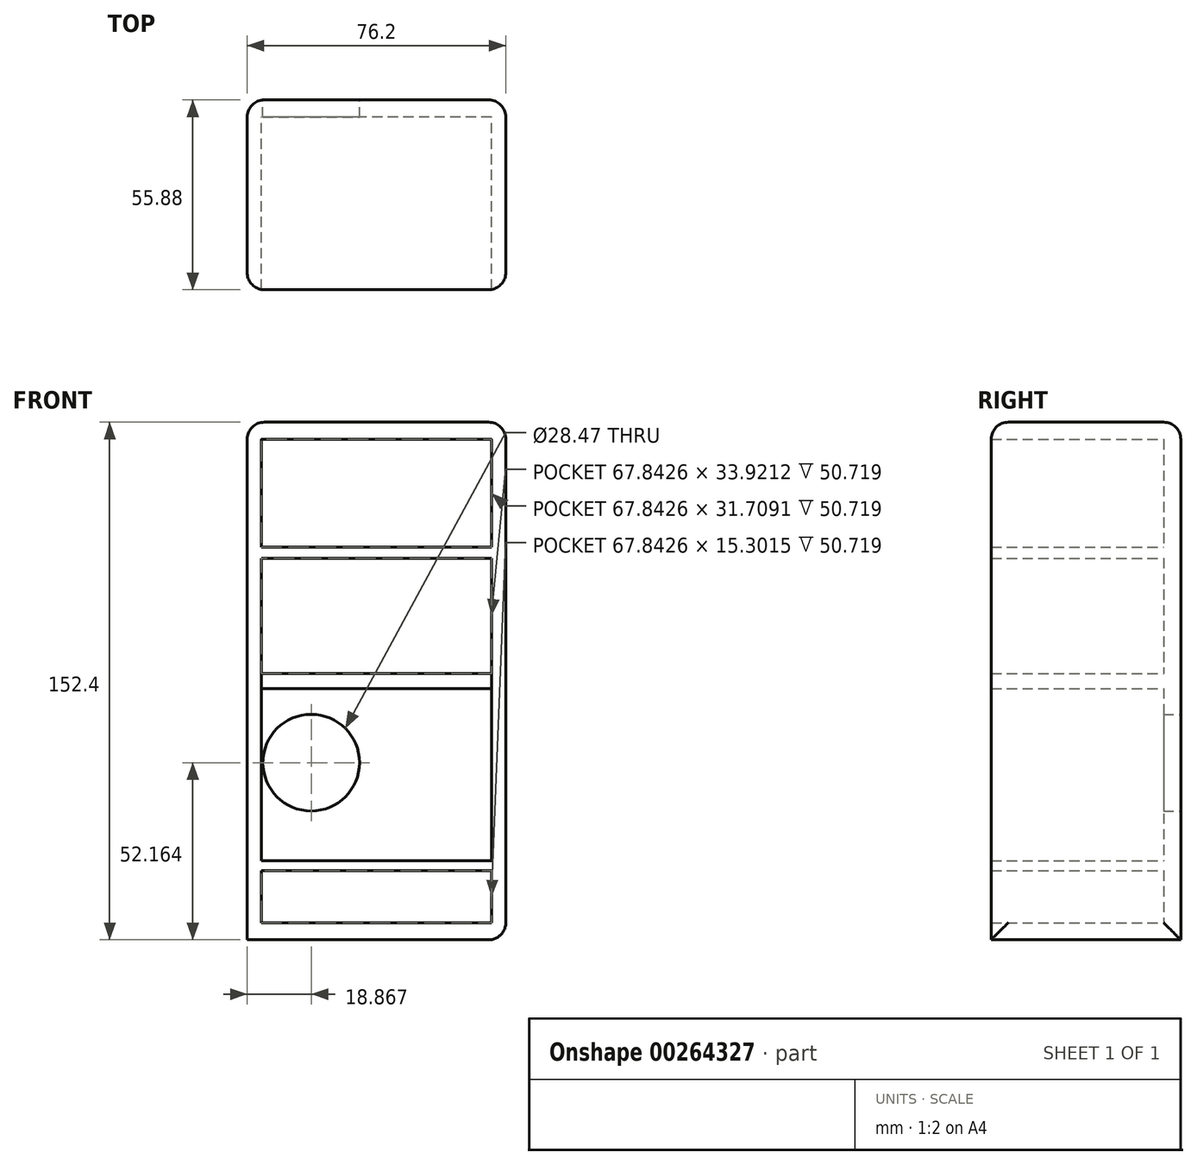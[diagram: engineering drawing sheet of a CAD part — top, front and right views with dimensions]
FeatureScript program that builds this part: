
annotation { "Feature Type Name" : "Feature", "Feature Type Description" : "" }
export const myFeature = defineFeature(function(context is Context, id is Id, definition is map)
    precondition{}
    {
        {
            var Q0;
            Q0=qCreatedBy(makeId("Front.planeOp"),FACE);
            var sketch = newSketch(context, id + "F0", { "sketchPlane" : qUnion([Q0])});
            skLineSegment(sketch, "E0.bottom", {"start": v(38.1, 76.2) * mm, "end": v(-38.1, 76.2) * mm});
            skLineSegment(sketch, "E0.top", {"start": v(38.1, -76.2) * mm, "end": v(-38.1, -76.2) * mm});
            skLineSegment(sketch, "E0.left", {"start": v(38.1, 76.2) * mm, "end": v(38.1, -76.2) * mm});
            skLineSegment(sketch, "E0.right", {"start": v(-38.1, 76.2) * mm, "end": v(-38.1, -76.2) * mm});
            skPoint(sketch, "E0.middle", {"position": v(0, 0) * mm});
            skLineSegment(sketch, "E1.bottom", {"start": v(33.92, 71.16) * mm, "end": v(-33.92, 71.16) * mm});
            skLineSegment(sketch, "E1.top", {"start": v(33.92, -71.16) * mm, "end": v(-33.92, -71.16) * mm});
            skLineSegment(sketch, "E1.left", {"start": v(33.92, 71.16) * mm, "end": v(33.92, -71.16) * mm});
            skLineSegment(sketch, "E1.right", {"start": v(-33.92, 71.16) * mm, "end": v(-33.92, -71.16) * mm});
            skLineSegment(sketch, "E2", {"start": v(-33.92, 39.45) * mm, "end": v(33.92, 39.45) * mm});
            skLineSegment(sketch, "E3", {"start": v(33.92, 39.45) * mm, "end": v(33.92, 36.13) * mm});
            skLineSegment(sketch, "E4", {"start": v(33.92, 36.13) * mm, "end": v(-33.92, 36.13) * mm});
            skLineSegment(sketch, "E5", {"start": v(-33.92, 36.13) * mm, "end": v(-33.92, -55.86) * mm});
            skLineSegment(sketch, "E6", {"start": v(-33.92, -55.86) * mm, "end": v(33.92, -55.86) * mm});
            skLineSegment(sketch, "E7", {"start": v(33.92, -55.86) * mm, "end": v(33.92, -52.9) * mm});
            skLineSegment(sketch, "E8", {"start": v(33.92, -52.9) * mm, "end": v(-33.92, -52.9) * mm});
            skSolve(sketch);
        }
        {
            var Q0;
            Q0=makeQuery(id+"F0.imprint","IMPRINT",FACE,{"disambiguationData":[TD([[makeQuery(id+"F0.imprint","IMPRINT",EDGE,{"derivedFrom":sQuery(id+"F0.wireOp",EDGE,"E0.bottom")}),1.0]])]});
            var Q1;
            {var subQ0=sQuery(id+"F0.wireOp",EDGE,"E2");Q1=makeQuery(id+"F0.imprint","IMPRINT",FACE,{"disambiguationData":[TD([[makeQuery(id+"F0.imprint","IMPRINT",EDGE,{"derivedFrom":subQ0}),-1.0]])]});}
            var Q2;
            {var subQ0=sQuery(id+"F0.wireOp",EDGE,"E6");Q2=makeQuery(id+"F0.imprint","IMPRINT",FACE,{"disambiguationData":[TD([[makeQuery(id+"F0.imprint","IMPRINT",EDGE,{"derivedFrom":subQ0}),1.0]])]});}
            extrude(context, id + "F1", {"entities" : qUnion([Q0, Q1, Q2]), "depth" : 50.8 * mm});
        }
        {
            var Q0;
            Q0=makeQuery(id+"F1.opExtrude","CAP_FACE",FACE,{"disambiguationData":[OSD([sQuery(id+"F0.wireOp",EDGE,"E0.bottom"),sQuery(id+"F0.wireOp",EDGE,"E0.top"),sQuery(id+"F0.wireOp",EDGE,"E0.left"),sQuery(id+"F0.wireOp",EDGE,"E0.right"),sQuery(id+"F0.wireOp",EDGE,"E1.bottom"),sQuery(id+"F0.wireOp",EDGE,"E1.top"),sQuery(id+"F0.wireOp",EDGE,"E1.left"),sQuery(id+"F0.wireOp",EDGE,"E1.right"),sQuery(id+"F0.wireOp",EDGE,"E2"),sQuery(id+"F0.wireOp",EDGE,"E4"),sQuery(id+"F0.wireOp",EDGE,"E5"),sQuery(id+"F0.wireOp",EDGE,"E6"),sQuery(id+"F0.wireOp",EDGE,"E8")])],"isStart":true});
            var sketch = newSketch(context, id + "F2", { "sketchPlane" : qUnion([Q0])});
            skLineSegment(sketch, "E9.bottom", {"start": v(-38.1, 76.2) * mm, "end": v(38.1, 76.2) * mm});
            skLineSegment(sketch, "E9.top", {"start": v(-38.1, -76.2) * mm, "end": v(38.1, -76.2) * mm});
            skLineSegment(sketch, "E9.left", {"start": v(-38.1, 76.2) * mm, "end": v(-38.1, -76.2) * mm});
            skLineSegment(sketch, "E9.right", {"start": v(38.1, 76.2) * mm, "end": v(38.1, -76.2) * mm});
            skSolve(sketch);
        }
        {
            var Q0;
            Q0=makeQuery(id+"F2.imprint","IMPRINT",FACE,{"disambiguationData":[TD([[makeQuery(id+"F2.imprint","IMPRINT",EDGE,{"derivedFrom":sQuery(id+"F2.wireOp",EDGE,"E9.bottom")}),-1.0]])]});
            var Q1;
            {var subQ0=sQuery(id+"F0.wireOp",EDGE,"E1.bottom");Q1=makeQuery(id+"F2.imprint","IMPRINT",FACE,{"disambiguationData":[TD([[makeQuery(id+"F2.imprint","IMPRINT",EDGE,{"derivedFrom":makeQuery(id+"F1.opExtrude","CAP_EDGE",EDGE,{"disambiguationData":[OSD([subQ0])],"isStart":true})}),-1.0]])]});}
            var Q2;
            {var subQ0=sQuery(id+"F0.wireOp",EDGE,"E1.top");Q2=makeQuery(id+"F2.imprint","IMPRINT",FACE,{"disambiguationData":[TD([[makeQuery(id+"F2.imprint","IMPRINT",EDGE,{"derivedFrom":makeQuery(id+"F1.opExtrude","CAP_EDGE",EDGE,{"disambiguationData":[OSD([subQ0])],"isStart":true})}),1.0]])]});}
            var Q3;
            {var subQ0=sQuery(id+"F0.wireOp",EDGE,"E4");Q3=makeQuery(id+"F2.imprint","IMPRINT",FACE,{"disambiguationData":[TD([[makeQuery(id+"F2.imprint","IMPRINT",EDGE,{"derivedFrom":makeQuery(id+"F1.opExtrude","CAP_EDGE",EDGE,{"disambiguationData":[OSD([subQ0])],"isStart":true})}),-1.0]])]});}
            extrude(context, id + "F3", {"entities" : qUnion([Q0, Q1, Q2, Q3]), "operationType" : NewBodyOperationType.ADD, "depth" : 5.08 * mm});
        }
        {
            var Q0;
            Q0=makeQuery(id+"F3.boolean.opBoolean","MERGE",FACE,{"derivedFrom":[makeQuery(id+"F1.opExtrude","SWEPT_FACE",FACE,{"disambiguationData":[OSD([sQuery(id+"F0.wireOp",EDGE,"E0.left")])]}),makeQuery(id+"F3.opExtrude","SWEPT_FACE",FACE,{"disambiguationData":[OSD([sQuery(id+"F2.wireOp",EDGE,"E9.left")])]})]});
            var Q1;
            Q1=makeQuery(id+"F3.opExtrude","CAP_EDGE",EDGE,{"disambiguationData":[OSD([sQuery(id+"F2.wireOp",EDGE,"E9.right")])],"isStart":false});
            var Q2;
            Q2=makeQuery(id+"F3.boolean.opBoolean","MERGE",EDGE,{"derivedFrom":[makeQuery(id+"F1.opExtrude","SWEPT_EDGE",EDGE,{"disambiguationData":[OSD([sQuery(id+"F0.wireOp",EDGE,"E0.bottom"),sQuery(id+"F0.wireOp",EDGE,"E0.right")])]}),makeQuery(id+"F3.opExtrude","SWEPT_EDGE",EDGE,{"disambiguationData":[OSD([sQuery(id+"F2.wireOp",EDGE,"E9.bottom"),sQuery(id+"F2.wireOp",EDGE,"E9.right")])]})]});
            fillet(context, id + "F4", {"entities" : qUnion([Q0, Q1, Q2]), "radius" : 5.08 * mm, "tangentPropagation" : true, "allowEdgeOverflow" : false});
        }
        {
            var Q0;
            Q0=makeQuery(id+"F3.opExtrude","CAP_EDGE",EDGE,{"disambiguationData":[OSD([sQuery(id+"F2.wireOp",EDGE,"E9.bottom")])],"isStart":false});
            fillet(context, id + "F5", {"entities" : qUnion([Q0]), "radius" : 5.08 * mm, "tangentPropagation" : true, "allowEdgeOverflow" : false});
        }
        {
            var Q0;
            Q0=makeQuery(id+"F1.opExtrude","CAP_EDGE",EDGE,{"disambiguationData":[OSD([sQuery(id+"F0.wireOp",EDGE,"E0.right")])],"isStart":false});
            fillet(context, id + "F6", {"entities" : qUnion([Q0]), "radius" : 5.08 * mm, "tangentPropagation" : true, "allowEdgeOverflow" : false});
        }
        {
            var Q0;
            {var subQ0=sQuery(id+"F0.wireOp",EDGE,"E4");Q0=makeQuery(id+"F3.boolean.opBoolean","SPLIT",FACE,{"disambiguationData":[TD([makeQuery(id+"F1.opExtrude","SWEPT_FACE",FACE,{"disambiguationData":[OSD([subQ0])]})])],"derivedFrom":makeQuery(id+"F3.opExtrude","CAP_FACE",FACE,{"disambiguationData":[OSD([sQuery(id+"F2.wireOp",EDGE,"E9.bottom"),sQuery(id+"F2.wireOp",EDGE,"E9.top"),sQuery(id+"F2.wireOp",EDGE,"E9.left"),sQuery(id+"F2.wireOp",EDGE,"E9.right")])],"isStart":true})});}
            var sketch = newSketch(context, id + "F7", { "sketchPlane" : qUnion([Q0])});
            skLineSegment(sketch, "E10.bottom", {"start": v(33.92, 2.21) * mm, "end": v(-33.92, 2.21) * mm});
            skLineSegment(sketch, "E10.top", {"start": v(33.92, -2.21) * mm, "end": v(-33.92, -2.21) * mm});
            skLineSegment(sketch, "E10.left", {"start": v(33.92, 2.21) * mm, "end": v(33.92, -2.21) * mm});
            skLineSegment(sketch, "E10.right", {"start": v(-33.92, 2.21) * mm, "end": v(-33.92, -2.21) * mm});
            skPoint(sketch, "E10.middle", {"position": v(0, 0) * mm});
            skSolve(sketch);
        }
        {
            var Q0;
            Q0=makeQuery(id+"F7.imprint","IMPRINT",FACE,{"disambiguationData":[TD([[makeQuery(id+"F7.imprint","IMPRINT",EDGE,{"derivedFrom":sQuery(id+"F7.wireOp",EDGE,"E10.bottom")}),1.0]])]});
            extrude(context, id + "F8", {"entities" : qUnion([Q0]), "operationType" : NewBodyOperationType.ADD, "depth" : 50.8 * mm});
        }
        {
            var Q0;
            Q0=makeQuery(id+"F3.opExtrude","CAP_FACE",FACE,{"disambiguationData":[OSD([sQuery(id+"F2.wireOp",EDGE,"E9.bottom"),sQuery(id+"F2.wireOp",EDGE,"E9.top"),sQuery(id+"F2.wireOp",EDGE,"E9.left"),sQuery(id+"F2.wireOp",EDGE,"E9.right")])],"isStart":false});
            var sketch = newSketch(context, id + "F9", { "sketchPlane" : qUnion([Q0])});
            skCircle(sketch, "E11", {"center": v(19.23, -24.04) * mm, "radius": 14.23 * mm});
            skSolve(sketch);
        }
        {
            var Q0;
            Q0 = qSketchRegion(id + "F9", true);
            extrude(context, id + "F10", {"entities" : qUnion([Q0]), "operationType" : NewBodyOperationType.REMOVE, "oppositeDirection" : true, "depth" : 25.4 * mm});
        }
    });
